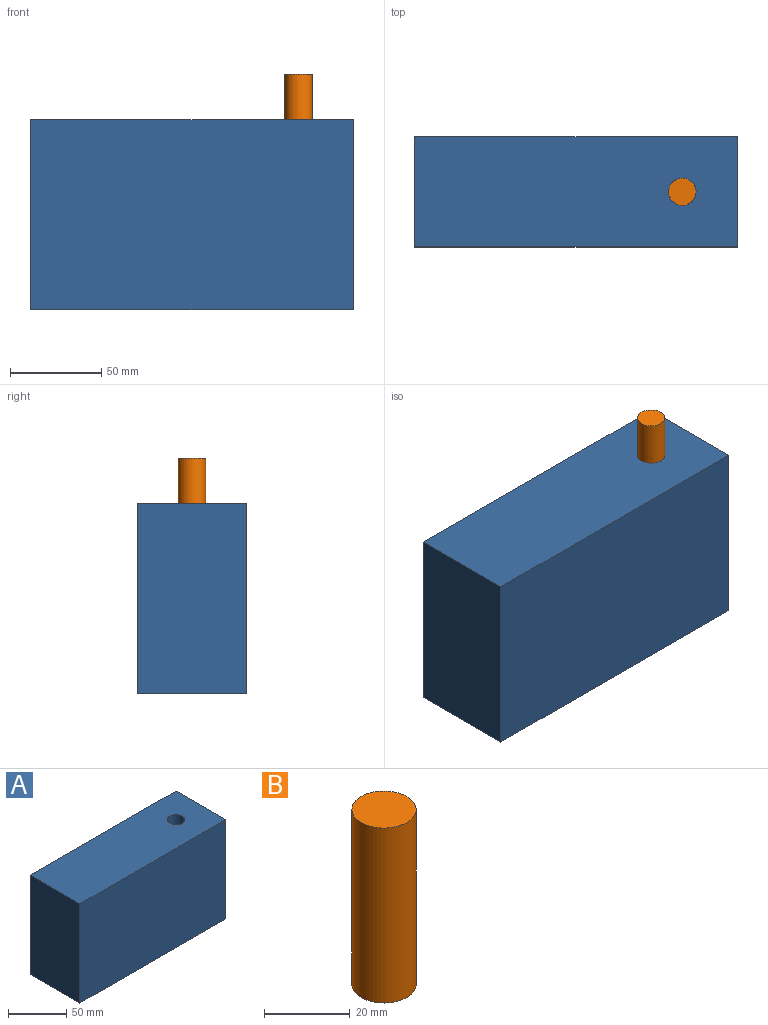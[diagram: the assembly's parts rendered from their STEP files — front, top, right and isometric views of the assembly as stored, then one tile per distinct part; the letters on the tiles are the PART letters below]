
ASSEMBLY  parts=2 mates=2
PART A: 7 faces, bbox 176.2x60x103.9 mm
  f0: plane 176.24x60mm, normal (0,0,1), area 10397.8mm2, adj f1,f3,f4,f5,f6
  f1: plane 103.9x60mm, normal (-1,0,0), area 6234.2mm2, adj f0,f2,f4,f5
  f2: plane 176.24x60mm, normal (0,0,-1), area 10397.8mm2, adj f1,f3,f4,f5,f6
  f3: plane 103.9x60mm, normal (1,0,0), area 6234.2mm2, adj f0,f2,f4,f5
  f4: plane 176.24x103.9mm, normal (0,-1,0), area 18312.3mm2, adj f0,f1,f2,f3
  f5: plane 176.24x103.9mm, normal (0,1,0), area 18312.3mm2, adj f0,f1,f2,f3
  f6: cylinder r=7.5mm len=103.9mm, axis (0,0,1), area 4896.4mm2, adj f0,f2
PART B: 3 faces, bbox 15x15x50 mm
  f0: cylinder r=7.5mm len=50mm, axis (0,0,-1), area 2356.2mm2, adj f1,f2
  f1: plane 15x15mm, normal (0,0,1), area 176.7mm2, adj f0
  f2: plane 15x15mm, normal (0,0,-1), area 176.7mm2, adj f0
PLACE A t=(-24.7,-17.2,-18.58)mm fixed
PLACE B rot(axis=(0.71,-0.71,0),180deg) t=(62.69,-17.2,47.19)mm
MATE slider B.f0 <-> B.f0  axis (0,0,1) through (62.69,-17.2,47.19)mm
MATE slider B.f0 <-> A.f6  axis (0,0,-1) through (62.69,-17.2,-2.81)mm
